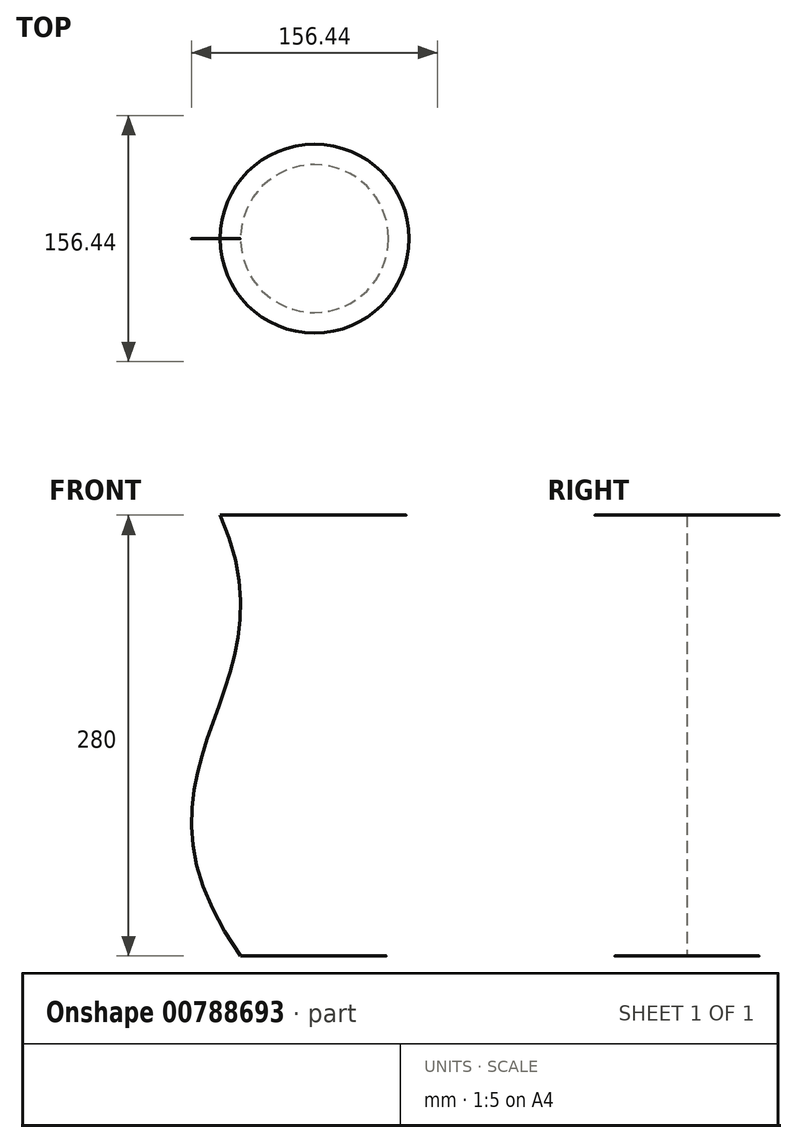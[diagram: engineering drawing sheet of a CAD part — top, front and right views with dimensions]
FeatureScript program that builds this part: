
annotation { "Feature Type Name" : "Feature", "Feature Type Description" : "" }
export const myFeature = defineFeature(function(context is Context, id is Id, definition is map)
    precondition{}
    {
        {
            var Q0;
            Q0=qCreatedBy(makeId("Front.planeOp"),FACE);
            var sketch = newSketch(context, id + "F0", { "sketchPlane" : qUnion([Q0])});
            skLineSegment(sketch, "E0", {"start": v(0, 0) * mm, "end": v(0, 280) * mm});
            skLineSegment(sketch, "E1", {"start": v(0, 0) * mm, "end": v(47, 0) * mm});
            skLineSegment(sketch, "E2", {"start": v(0, 280) * mm, "end": v(60, 280) * mm});
            skFitSpline(sketch, "E3", {"points": [v(60, 280) * mm, v(47, 0) * mm], "startDerivative": vector(-154.96, -344.36) * mm, "endDerivative": vector(-258.1, -368.62) * mm});
            skLineSegment(sketch, "E4", {"start": v(47, 0) * mm, "end": v(47, 241.11) * mm, "construction": true});
            skPoint(sketch, "E5", {"position": v(47, 225) * mm});
            skLineSegment(sketch, "E6", {"start": v(47, 0) * mm, "end": v(164.2, 167.38) * mm, "construction": true});
            skLineSegment(sketch, "E7", {"start": v(60, 280) * mm, "end": v(-110.18, 109.82) * mm, "construction": true});
            skLineSegment(sketch, "E8", {"start": v(83.32, 0) * mm, "end": v(83.32, 280) * mm, "construction": true});
            skSolve(sketch);
        }
        {
            var Q0;
            Q0=makeQuery(id+"F0.imprint","IMPRINT",FACE,{"disambiguationData":[TD([[makeQuery(id+"F0.imprint","IMPRINT",EDGE,{"derivedFrom":sQuery(id+"F0.wireOp",EDGE,"E0")}),-1.0]])]});
            var Q1;
            Q1=sQuery(id+"F0.wireOp",EDGE,"E0");
            revolve(context, id + "F1", {"surfaceOperationType" : NewSurfaceOperationType.NEW, "entities" : qUnion([Q0]), "axis" : qUnion([Q1]), "revolveType" : RevolveType.FULL});
        }
    });
